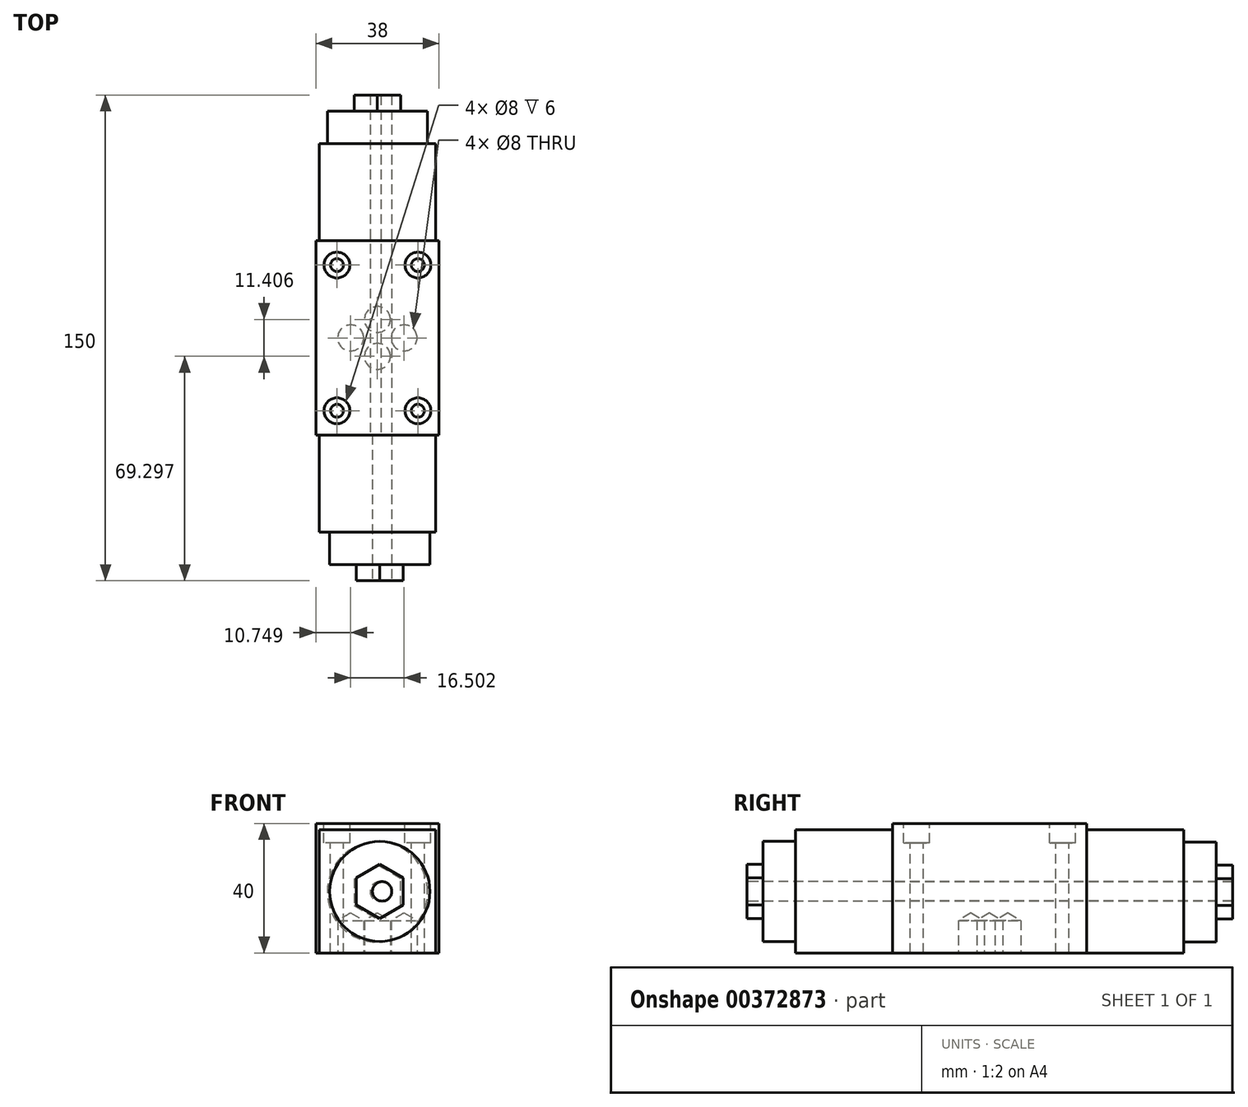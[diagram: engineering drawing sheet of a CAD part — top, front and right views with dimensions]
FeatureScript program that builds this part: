
annotation { "Feature Type Name" : "Feature", "Feature Type Description" : "" }
export const myFeature = defineFeature(function(context is Context, id is Id, definition is map)
    precondition{}
    {
        {
            var Q0;
            Q0=qCreatedBy(makeId("Top.planeOp"),FACE);
            var sketch = newSketch(context, id + "F0", { "sketchPlane" : qUnion([Q0])});
            skLineSegment(sketch, "E0.bottom", {"start": v(-19, 30) * mm, "end": v(19, 30) * mm});
            skLineSegment(sketch, "E0.top", {"start": v(-19, -30) * mm, "end": v(19, -30) * mm});
            skLineSegment(sketch, "E0.left", {"start": v(-19, 30) * mm, "end": v(-19, -30) * mm});
            skLineSegment(sketch, "E0.right", {"start": v(19, 30) * mm, "end": v(19, -30) * mm});
            skPoint(sketch, "E0.middle", {"position": v(0, 0) * mm});
            skSolve(sketch);
        }
        {
            var Q0;
            Q0=makeQuery(id+"F0.imprint","IMPRINT",FACE,{"disambiguationData":[TD([[makeQuery(id+"F0.imprint","IMPRINT",EDGE,{"derivedFrom":sQuery(id+"F0.wireOp",EDGE,"E0.bottom")}),-1.0]])]});
            extrude(context, id + "F1", {"entities" : qUnion([Q0]), "depth" : 40 * mm});
        }
        {
            var Q0;
            Q0=makeQuery(id+"F1.opExtrude","CAP_FACE",FACE,{"disambiguationData":[OSD([sQuery(id+"F0.wireOp",EDGE,"E0.bottom"),sQuery(id+"F0.wireOp",EDGE,"E0.top"),sQuery(id+"F0.wireOp",EDGE,"E0.left"),sQuery(id+"F0.wireOp",EDGE,"E0.right")])],"isStart":false});
            var sketch = newSketch(context, id + "F2", { "sketchPlane" : qUnion([Q0])});
            skLineSegment(sketch, "E1.bottom", {"start": v(-12.5, 22.5) * mm, "end": v(12.5, 22.5) * mm});
            skLineSegment(sketch, "E1.top", {"start": v(-12.5, -22.5) * mm, "end": v(12.5, -22.5) * mm});
            skLineSegment(sketch, "E1.left", {"start": v(-12.5, 22.5) * mm, "end": v(-12.5, -22.5) * mm});
            skLineSegment(sketch, "E1.right", {"start": v(12.5, 22.5) * mm, "end": v(12.5, -22.5) * mm});
            skPoint(sketch, "E1.middle", {"position": v(0, 0) * mm});
            skSolve(sketch);
        }
        {
            var Q0;
            Q0=sQuery(id+"F2.wireOp",VERTEX,"E1.left.start");
            var Q1;
            Q1=sQuery(id+"F2.wireOp",VERTEX,"E1.right.start");
            var Q2;
            Q2=sQuery(id+"F2.wireOp",VERTEX,"E1.top.end");
            var Q3;
            Q3=sQuery(id+"F2.wireOp",VERTEX,"E1.left.end");
            var Q4;
            Q4=makeQuery(id+"F1.opExtrude","SWEPT_BODY",BODY,{"disambiguationData":[OSD([sQuery(id+"F0.wireOp",EDGE,"E0.bottom"),sQuery(id+"F0.wireOp",EDGE,"E0.top"),sQuery(id+"F0.wireOp",EDGE,"E0.left"),sQuery(id+"F0.wireOp",EDGE,"E0.right")])]});
            hole(context, id + "F3", {"style" : HoleStyle.C_BORE, "endStyle" : HoleEndStyle.THROUGH, "holeDiameter" : 4 * mm, "cBoreDiameter" : 8 * mm, "cBoreDepth" : 6 * mm, "isTappedThrough" : true, "tappedDepth" : 12 * mm, "tapClearance" : 3, "startFromSketch" : true, "locations" : qUnion([Q0, Q1, Q2, Q3]), "scope" : qUnion([Q4])});
        }
        {
            var Q0;
            Q0=makeQuery(id+"F1.opExtrude","CAP_FACE",FACE,{"disambiguationData":[OSD([sQuery(id+"F0.wireOp",EDGE,"E0.bottom"),sQuery(id+"F0.wireOp",EDGE,"E0.top"),sQuery(id+"F0.wireOp",EDGE,"E0.left"),sQuery(id+"F0.wireOp",EDGE,"E0.right")])],"isStart":true});
            var sketch = newSketch(context, id + "F4", { "sketchPlane" : qUnion([Q0])});
            skLineSegment(sketch, "E2.bottom", {"start": v(-8.25, 5.7) * mm, "end": v(8.25, 5.7) * mm});
            skLineSegment(sketch, "E2.top", {"start": v(-8.25, -5.7) * mm, "end": v(8.25, -5.7) * mm});
            skLineSegment(sketch, "E2.left", {"start": v(-8.25, 5.7) * mm, "end": v(-8.25, -5.7) * mm});
            skLineSegment(sketch, "E2.right", {"start": v(8.25, 5.7) * mm, "end": v(8.25, -5.7) * mm});
            skPoint(sketch, "E2.middle", {"position": v(0, 0) * mm});
            skPoint(sketch, "E3", {"position": v(0, 5.7) * mm});
            skPoint(sketch, "E4", {"position": v(0, -5.7) * mm});
            skPoint(sketch, "E5", {"position": v(8.25, 0) * mm});
            skPoint(sketch, "E6", {"position": v(-8.25, 0) * mm});
            skSolve(sketch);
        }
        {
            var Q0;
            Q0=sQuery(id+"F4.wireOp",VERTEX,"E3");
            var Q1;
            Q1=sQuery(id+"F4.wireOp",VERTEX,"E6");
            var Q2;
            Q2=sQuery(id+"F4.wireOp",VERTEX,"E4");
            var Q3;
            Q3=sQuery(id+"F4.wireOp",VERTEX,"E5");
            var Q4;
            Q4=makeQuery(id+"F1.opExtrude","SWEPT_BODY",BODY,{"disambiguationData":[OSD([sQuery(id+"F0.wireOp",EDGE,"E0.bottom"),sQuery(id+"F0.wireOp",EDGE,"E0.top"),sQuery(id+"F0.wireOp",EDGE,"E0.left"),sQuery(id+"F0.wireOp",EDGE,"E0.right")])]});
            hole(context, id + "F5", {"style" : HoleStyle.SIMPLE, "endStyle" : HoleEndStyle.BLIND, "holeDiameter" : 8 * mm, "holeDepth" : 10 * mm, "isTappedThrough" : true, "tappedDepth" : 12 * mm, "tapClearance" : 3, "startFromSketch" : true, "locations" : qUnion([Q0, Q1, Q2, Q3]), "scope" : qUnion([Q4])});
        }
        {
            var Q0;
            Q0=makeQuery(id+"F1.opExtrude","CAP_FACE",FACE,{"disambiguationData":[OSD([sQuery(id+"F0.wireOp",EDGE,"E0.bottom"),sQuery(id+"F0.wireOp",EDGE,"E0.top"),sQuery(id+"F0.wireOp",EDGE,"E0.left"),sQuery(id+"F0.wireOp",EDGE,"E0.right")])],"isStart":true});
            var sketch = newSketch(context, id + "F6", { "sketchPlane" : qUnion([Q0])});
            skLineSegment(sketch, "E7.bottom", {"start": v(18, 0) * mm, "end": v(-18, 0) * mm});
            skLineSegment(sketch, "E7.top", {"start": v(18, -60) * mm, "end": v(-18, -60) * mm});
            skLineSegment(sketch, "E7.left", {"start": v(18, 0) * mm, "end": v(18, -60) * mm});
            skLineSegment(sketch, "E7.right", {"start": v(-18, 0) * mm, "end": v(-18, -60) * mm});
            skPoint(sketch, "E7.middle", {"position": v(0, -30) * mm});
            skPoint(sketch, "E7.cornerSnap0", {"position": v(19, 0) * mm});
            skSolve(sketch);
        }
        {
            var Q0;
            {var subQ0=sQuery(id+"F6.wireOp",EDGE,"E7.top");Q0=makeQuery(id+"F6.imprint","IMPRINT",FACE,{"disambiguationData":[TD([[makeQuery(id+"F6.imprint","IMPRINT",EDGE,{"derivedFrom":subQ0}),-1.0]])]});}
            extrude(context, id + "F7", {"entities" : qUnion([Q0]), "operationType" : NewBodyOperationType.ADD, "oppositeDirection" : true, "depth" : 38 * mm});
        }
        {
            var Q0;
            Q0=makeQuery(id+"F7.opExtrude","SWEPT_FACE",FACE,{"disambiguationData":[OSD([sQuery(id+"F6.wireOp",EDGE,"E7.top")])]});
            var sketch = newSketch(context, id + "F8", { "sketchPlane" : qUnion([Q0])});
            skCircle(sketch, "E8", {"center": v(0, 18.8) * mm, "radius": 15.48 * mm});
            skCircle(sketch, "E9", {"center": v(0, 18.8) * mm, "radius": 2 * mm});
            skCircle(sketch, "E10.cCircle", {"center": v(0, 18.8) * mm, "radius": 7.23 * mm, "construction": true});
            skLineSegment(sketch, "E10.0", {"start": v(-7.23, 14.63) * mm, "end": v(-7.23, 22.98) * mm});
            skLineSegment(sketch, "E10.1", {"start": v(-7.23, 22.98) * mm, "end": v(0, 27.16) * mm});
            skLineSegment(sketch, "E10.2", {"start": v(0, 27.16) * mm, "end": v(7.23, 22.98) * mm});
            skLineSegment(sketch, "E10.3", {"start": v(7.23, 22.98) * mm, "end": v(7.23, 14.63) * mm});
            skLineSegment(sketch, "E10.4", {"start": v(7.23, 14.63) * mm, "end": v(0, 10.46) * mm});
            skLineSegment(sketch, "E10.5", {"start": v(0, 10.46) * mm, "end": v(-7.23, 14.63) * mm});
            skPoint(sketch, "E10.0.midPoint", {"position": v(-7.23, 18.8) * mm});
            skSolve(sketch);
        }
        {
            var Q0;
            Q0 = qSketchRegion(id + "F8", true);
            extrude(context, id + "F9", {"entities" : qUnion([Q0]), "operationType" : NewBodyOperationType.ADD, "depth" : 10 * mm});
        }
        {
            var Q0;
            {var subQ0=sQuery(id+"F0.wireOp",EDGE,"E0.bottom");Q0=makeQuery(id+"F7.boolean.opBoolean","MERGE",FACE,{"derivedFrom":[makeQuery(id+"F1.opExtrude","CAP_FACE",FACE,{"disambiguationData":[OSD([subQ0,sQuery(id+"F0.wireOp",EDGE,"E0.top"),sQuery(id+"F0.wireOp",EDGE,"E0.left"),sQuery(id+"F0.wireOp",EDGE,"E0.right")])],"isStart":true}),makeQuery(id+"F7.opExtrude","CAP_FACE",FACE,{"disambiguationData":[OSD([subQ0,sQuery(id+"F6.wireOp",EDGE,"E7.top"),sQuery(id+"F6.wireOp",EDGE,"E7.left"),sQuery(id+"F6.wireOp",EDGE,"E7.right")])],"isStart":true})]});}
            var sketch = newSketch(context, id + "F10", { "sketchPlane" : qUnion([Q0])});
            skLineSegment(sketch, "E11.bottom", {"start": v(18, 60) * mm, "end": v(-18, 60) * mm});
            skLineSegment(sketch, "E11.top", {"start": v(18, 0) * mm, "end": v(-18, 0) * mm});
            skLineSegment(sketch, "E11.left", {"start": v(18, 60) * mm, "end": v(18, 0) * mm});
            skLineSegment(sketch, "E11.right", {"start": v(-18, 60) * mm, "end": v(-18, 0) * mm});
            skPoint(sketch, "E11.middle", {"position": v(0, 30) * mm});
            skPoint(sketch, "E11.cornerSnap0", {"position": v(15.83, 60) * mm});
            skSolve(sketch);
        }
        {
            var Q0;
            {var subQ0=sQuery(id+"F10.wireOp",EDGE,"E11.bottom");Q0=makeQuery(id+"F10.imprint","IMPRINT",FACE,{"disambiguationData":[TD([[makeQuery(id+"F10.imprint","IMPRINT",EDGE,{"derivedFrom":subQ0}),1.0]])]});}
            extrude(context, id + "F11", {"entities" : qUnion([Q0]), "oppositeDirection" : true, "depth" : 38 * mm});
        }
        {
            var Q0;
            Q0=makeQuery(id+"F11.opExtrude","SWEPT_FACE",FACE,{"disambiguationData":[OSD([sQuery(id+"F10.wireOp",EDGE,"E11.bottom")])]});
            var sketch = newSketch(context, id + "F12", { "sketchPlane" : qUnion([Q0])});
            skCircle(sketch, "E12", {"center": v(0.72, 19) * mm, "radius": 15.48 * mm});
            skCircle(sketch, "E13", {"center": v(0.72, 19) * mm, "radius": 2 * mm});
            skCircle(sketch, "E14.cCircle", {"center": v(0.72, 19) * mm, "radius": 7.23 * mm, "construction": true});
            skLineSegment(sketch, "E14.0", {"start": v(-6.5, 14.82) * mm, "end": v(-6.5, 23.18) * mm});
            skLineSegment(sketch, "E14.1", {"start": v(-6.5, 23.18) * mm, "end": v(0.72, 27.35) * mm});
            skLineSegment(sketch, "E14.2", {"start": v(0.72, 27.35) * mm, "end": v(7.96, 23.18) * mm});
            skLineSegment(sketch, "E14.3", {"start": v(7.96, 23.18) * mm, "end": v(7.96, 14.82) * mm});
            skLineSegment(sketch, "E14.4", {"start": v(7.96, 14.82) * mm, "end": v(0.72, 10.65) * mm});
            skLineSegment(sketch, "E14.5", {"start": v(0.72, 10.65) * mm, "end": v(-6.5, 14.82) * mm});
            skPoint(sketch, "E14.0.midPoint", {"position": v(-6.5, 19) * mm});
            skSolve(sketch);
        }
        {
            var Q0;
            Q0 = qSketchRegion(id + "F12", true);
            extrude(context, id + "F13", {"entities" : qUnion([Q0]), "operationType" : NewBodyOperationType.ADD, "depth" : 10 * mm});
        }
        {
            var Q0;
            Q0=makeQuery(id+"F13.boolean.opBoolean","SPLIT",FACE,{"disambiguationData":[TD([makeQuery(id+"F13.opExtrude","SWEPT_FACE",FACE,{"disambiguationData":[OSD([sQuery(id+"F12.wireOp",EDGE,"E14.0")])]})])],"derivedFrom":makeQuery(id+"F11.opExtrude","SWEPT_FACE",FACE,{"disambiguationData":[OSD([sQuery(id+"F10.wireOp",EDGE,"E11.bottom")])]})});
            extrude(context, id + "F14", {"entities" : qUnion([Q0]), "operationType" : NewBodyOperationType.ADD, "depth" : 15 * mm});
        }
        {
            var Q0;
            Q0=makeQuery(id+"F9.boolean.opBoolean","SPLIT",FACE,{"disambiguationData":[TD([makeQuery(id+"F9.opExtrude","SWEPT_FACE",FACE,{"disambiguationData":[OSD([sQuery(id+"F8.wireOp",EDGE,"E10.0")])]})])],"derivedFrom":makeQuery(id+"F7.opExtrude","SWEPT_FACE",FACE,{"disambiguationData":[OSD([sQuery(id+"F6.wireOp",EDGE,"E7.top")])]})});
            extrude(context, id + "F15", {"entities" : qUnion([Q0]), "operationType" : NewBodyOperationType.ADD, "depth" : 15 * mm});
        }
        {
            var Q0;
            Q0=sQuery(id+"F12.wireOp",VERTEX,"E12.center");
            var Q1;
            Q1=makeQuery(id+"F1.opExtrude","SWEPT_BODY",BODY,{"disambiguationData":[OSD([sQuery(id+"F0.wireOp",EDGE,"E0.bottom"),sQuery(id+"F0.wireOp",EDGE,"E0.top"),sQuery(id+"F0.wireOp",EDGE,"E0.left"),sQuery(id+"F0.wireOp",EDGE,"E0.right")])]});
            hole(context, id + "F16", {"style" : HoleStyle.SIMPLE, "endStyle" : HoleEndStyle.THROUGH, "holeDiameter" : 6 * mm, "isTappedThrough" : true, "tappedDepth" : 12 * mm, "tapClearance" : 3, "startFromSketch" : true, "locations" : qUnion([Q0]), "scope" : qUnion([Q1])});
        }
        {
            var Q0;
            Q0=makeQuery(id+"F14.opExtrude","CAP_FACE",FACE,{"disambiguationData":[OSD([sQuery(id+"F10.wireOp",EDGE,"E11.bottom")])],"isStart":false});
            var sketch = newSketch(context, id + "F17", { "sketchPlane" : qUnion([Q0])});
            skCircle(sketch, "E15", {"center": v(1.45, 19) * mm, "radius": 15.48 * mm});
            skCircle(sketch, "E16", {"center": v(1.45, 19) * mm, "radius": 2 * mm});
            skCircle(sketch, "E17.cCircle", {"center": v(1.45, 19) * mm, "radius": 7.23 * mm, "construction": true});
            skLineSegment(sketch, "E17.0", {"start": v(-5.79, 14.82) * mm, "end": v(-5.79, 23.18) * mm});
            skLineSegment(sketch, "E17.1", {"start": v(-5.79, 23.18) * mm, "end": v(1.45, 27.35) * mm});
            skLineSegment(sketch, "E17.2", {"start": v(1.45, 27.35) * mm, "end": v(8.68, 23.18) * mm});
            skLineSegment(sketch, "E17.3", {"start": v(8.68, 23.18) * mm, "end": v(8.68, 14.82) * mm});
            skLineSegment(sketch, "E17.4", {"start": v(8.68, 14.82) * mm, "end": v(1.45, 10.65) * mm});
            skLineSegment(sketch, "E17.5", {"start": v(1.45, 10.65) * mm, "end": v(-5.79, 14.82) * mm});
            skPoint(sketch, "E17.0.midPoint", {"position": v(-5.79, 19) * mm});
            skSolve(sketch);
        }
        {
            var Q0;
            Q0=sQuery(id+"F17.wireOp",VERTEX,"E15.center");
            var Q1;
            Q1=makeQuery(id+"F1.opExtrude","SWEPT_BODY",BODY,{"disambiguationData":[OSD([sQuery(id+"F0.wireOp",EDGE,"E0.bottom"),sQuery(id+"F0.wireOp",EDGE,"E0.top"),sQuery(id+"F0.wireOp",EDGE,"E0.left"),sQuery(id+"F0.wireOp",EDGE,"E0.right")])]});
            var Q2;
            Q2=makeQuery(id+"F11.opExtrude","SWEPT_BODY",BODY,{"disambiguationData":[OSD([sQuery(id+"F0.wireOp",EDGE,"E0.top"),sQuery(id+"F10.wireOp",EDGE,"E11.bottom"),sQuery(id+"F10.wireOp",EDGE,"E11.left"),sQuery(id+"F10.wireOp",EDGE,"E11.right")])]});
            hole(context, id + "F18", {"style" : HoleStyle.SIMPLE, "endStyle" : HoleEndStyle.THROUGH, "holeDiameter" : 6 * mm, "isTappedThrough" : true, "tappedDepth" : 12 * mm, "tapClearance" : 3, "startFromSketch" : true, "locations" : qUnion([Q0]), "scope" : qUnion([Q1, Q2])});
        }
    });
